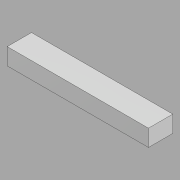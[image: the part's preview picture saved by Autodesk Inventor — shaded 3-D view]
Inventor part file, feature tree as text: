
AUTODESK INVENTOR PART (.ipt)
format: ipt  version: 2022.2 (Build 262287010, 287A)  size: 105,472 bytes
history: native  units: in
note: dims shown in document units (in); Inventor stores cm internally (conversion verified against a paired STEP export)
features: direct_edit x1, other x1, revolve x1
ambient origin geometry x8: Origin, YZ Plane, XZ Plane, XY Plane, X Axis, Y Axis, Z Axis, Center Point
bodies: Solid1 (feature_tree)
feature tree (3):
  direct_edit  "Direct Edit1"
  other  "L Vert rect jamb bottom_"
  revolve  "Rotate1"  Angle=90.0deg
